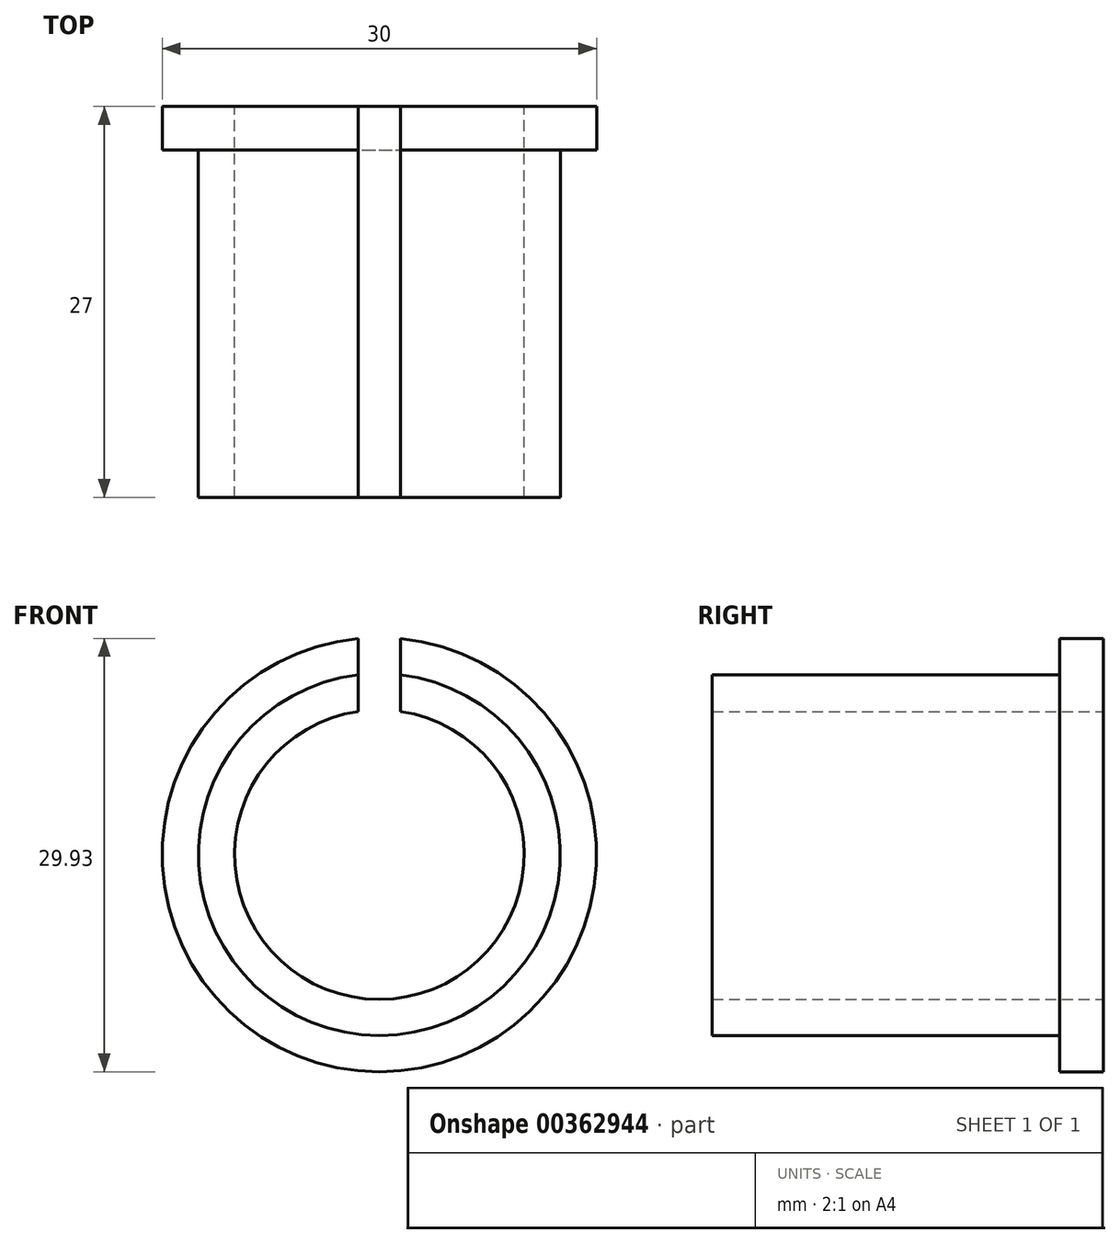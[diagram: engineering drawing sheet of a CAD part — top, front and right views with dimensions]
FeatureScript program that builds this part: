
annotation { "Feature Type Name" : "Feature", "Feature Type Description" : "" }
export const myFeature = defineFeature(function(context is Context, id is Id, definition is map)
    precondition{}
    {
        {
            var Q0;
            Q0=qCreatedBy(makeId("Front.planeOp"),FACE);
            var sketch = newSketch(context, id + "F0", { "sketchPlane" : qUnion([Q0])});
            skArc(sketch, "E0", {"start": v(-1.46, 9.9) * mm, "mid": v(0, -10) * mm, "end": v(1.46, 9.9) * mm});
            skArc(sketch, "E1", {"start": v(-1.46, 12.41) * mm, "mid": v(0, -12.5) * mm, "end": v(1.46, 12.41) * mm});
            skLineSegment(sketch, "E2", {"start": v(-1.46, 12.41) * mm, "end": v(-1.46, 9.9) * mm});
            skLineSegment(sketch, "E3.MirrorCS", {"start": v(1.46, 12.41) * mm, "end": v(1.46, 9.9) * mm});
            skArc(sketch, "E4", {"start": v(-1.46, 14.93) * mm, "mid": v(0, -15) * mm, "end": v(1.46, 14.93) * mm});
            skLineSegment(sketch, "E5", {"start": v(0, 0) * mm, "end": v(0, 17.5) * mm, "construction": true});
            skLineSegment(sketch, "E6", {"start": v(0, 17.5) * mm, "end": v(0, 16.3) * mm, "construction": true});
            skLineSegment(sketch, "E7", {"start": v(-1.46, 12.41) * mm, "end": v(-1.46, 14.93) * mm});
            skLineSegment(sketch, "E8.MirrorCS", {"start": v(1.46, 9.9) * mm, "end": v(1.46, 14.93) * mm});
            skSolve(sketch);
        }
        {
            var Q0;
            {var subQ0=sQuery(id+"F0.wireOp",EDGE,"E0");Q0=makeQuery(id+"F0.imprint","IMPRINT",FACE,{"disambiguationData":[TD([[makeQuery(id+"F0.imprint","IMPRINT",EDGE,{"derivedFrom":subQ0}),-1.0]])]});}
            extrude(context, id + "F1", {"entities" : qUnion([Q0]), "depth" : 27 * mm});
        }
        {
            var Q0;
            {var subQ0=sQuery(id+"F0.wireOp",EDGE,"E1");Q0=makeQuery(id+"F0.imprint","IMPRINT",FACE,{"disambiguationData":[TD([[makeQuery(id+"F0.imprint","IMPRINT",EDGE,{"derivedFrom":subQ0}),-1.0]])]});}
            extrude(context, id + "F2", {"entities" : qUnion([Q0]), "operationType" : NewBodyOperationType.ADD, "depth" : 3 * mm});
        }
    });
